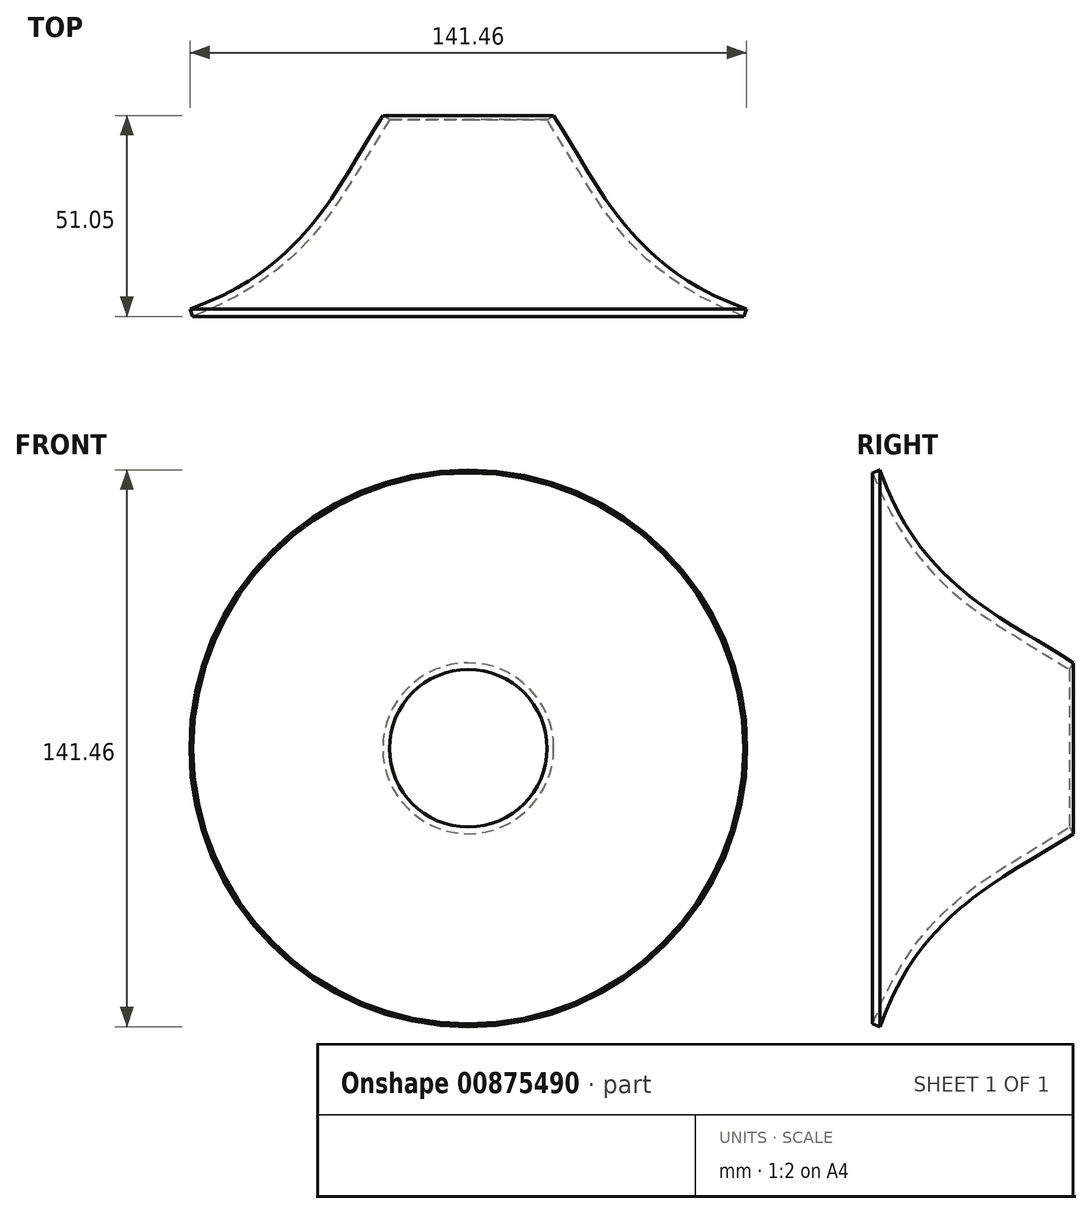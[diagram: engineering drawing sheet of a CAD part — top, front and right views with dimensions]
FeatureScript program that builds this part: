
annotation { "Feature Type Name" : "Feature", "Feature Type Description" : "" }
export const myFeature = defineFeature(function(context is Context, id is Id, definition is map)
    precondition{}
    {
        {
            var Q0;
            Q0=qCreatedBy(makeId("Right.planeOp"),FACE);
            var sketch = newSketch(context, id + "F0", { "sketchPlane" : qUnion([Q0])});
            skFitSpline(sketch, "E0", {"points": [v(0, 70) * mm, v(20, 40) * mm, v(50, 20) * mm], "startDerivative": vector(34.97, -89.58) * mm, "endDerivative": vector(90.9, -56.27) * mm});
            skLineSegment(sketch, "E1", {"start": v(0, 0) * mm, "end": v(-135.22, 0) * mm, "construction": true});
            skLineSegment(sketch, "E2", {"start": v(0, 0) * mm, "end": v(0, 106.78) * mm, "construction": true});
            skFitSpline(sketch, "E3.0", {"points": [v(1.86, 70.73) * mm, v(3.3, 67.06) * mm, v(6.28, 60.52) * mm, v(11.07, 52.69) * mm, v(15.25, 47.48) * mm, v(18.7, 43.9) * mm, v(21.32, 41.46) * mm, v(23.98, 39.22) * mm, v(27.7, 36.38) * mm, v(34.93, 31.5) * mm, v(43.46, 26.4) * mm, v(51.05, 21.7) * mm]});
            skLineSegment(sketch, "E4", {"start": v(0, 70) * mm, "end": v(1.86, 70.73) * mm});
            skLineSegment(sketch, "E5", {"start": v(50, 20) * mm, "end": v(51.05, 21.7) * mm});
            skSolve(sketch);
        }
        {
            var Q0;
            Q0=makeQuery(id+"F0.imprint","IMPRINT",FACE,{"disambiguationData":[TD([[makeQuery(id+"F0.imprint","IMPRINT",EDGE,{"derivedFrom":sQuery(id+"F0.wireOp",EDGE,"E0")}),1.0]])]});
            var Q1;
            Q1=sQuery(id+"F0.wireOp",EDGE,"E1");
            revolve(context, id + "F1", {"surfaceOperationType" : NewSurfaceOperationType.NEW, "entities" : qUnion([Q0]), "axis" : qUnion([Q1]), "revolveType" : RevolveType.FULL});
        }
    });
